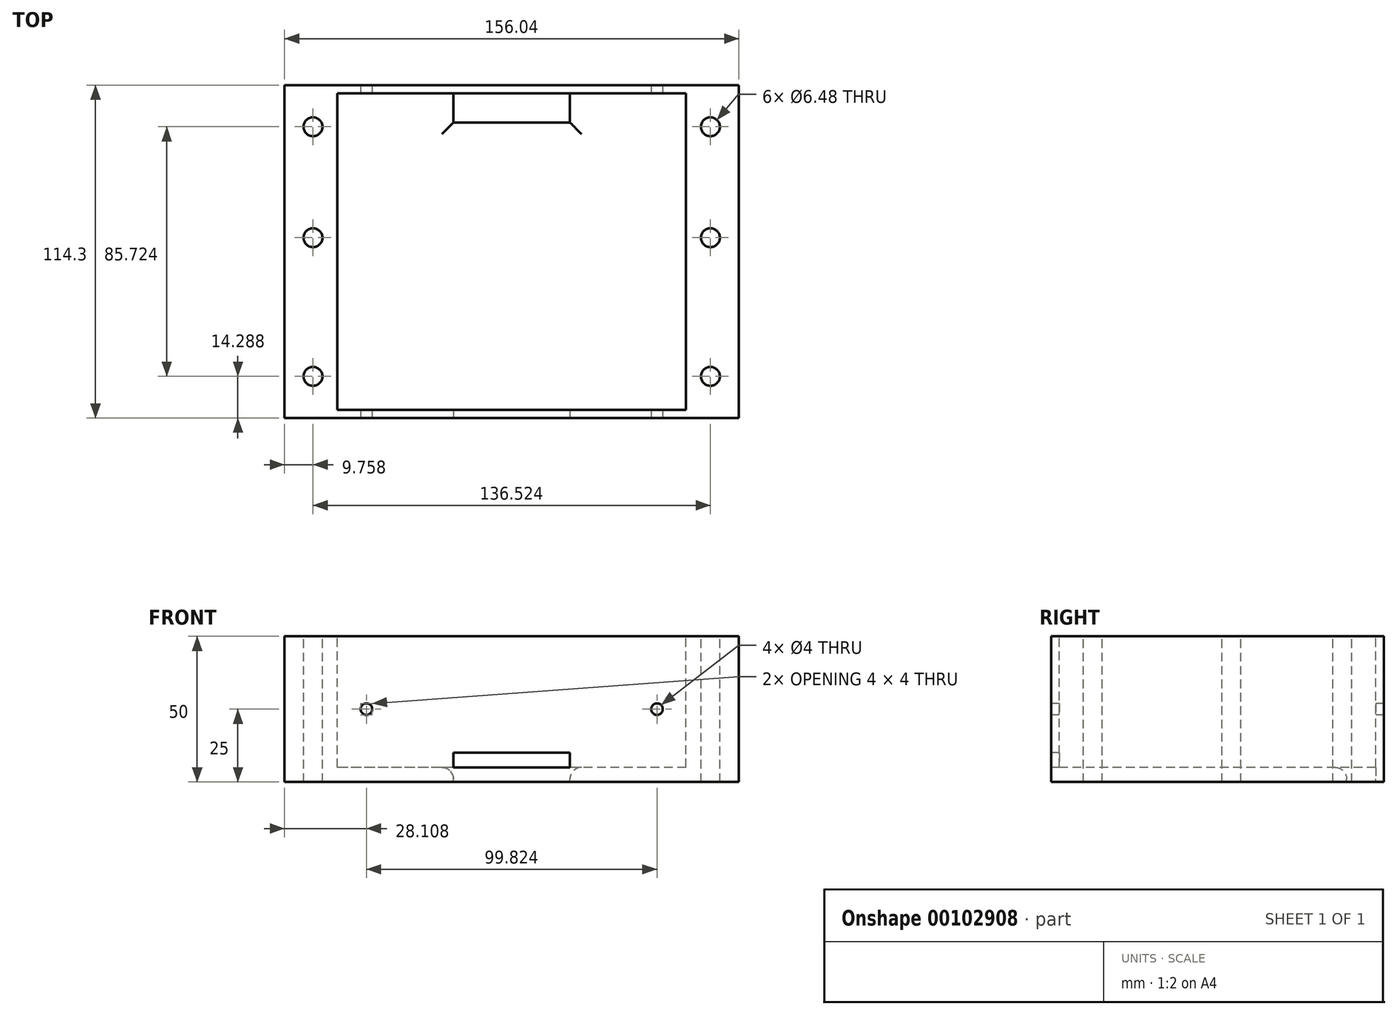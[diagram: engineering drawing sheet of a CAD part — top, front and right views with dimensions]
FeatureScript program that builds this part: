
annotation { "Feature Type Name" : "Feature", "Feature Type Description" : "" }
export const myFeature = defineFeature(function(context is Context, id is Id, definition is map)
    precondition{}
    {
        {
            var Q0;
            Q0=qCreatedBy(makeId("Top.planeOp"),FACE);
            var sketch = newSketch(context, id + "F0", { "sketchPlane" : qUnion([Q0])});
            skArc(sketch, "E0", {"start": v(-68.26, -1.59) * mm, "mid": v(-61.91, 4.76) * mm, "end": v(-68.26, 11.11) * mm});
            skArc(sketch, "E1", {"start": v(68.26, 11.11) * mm, "mid": v(61.91, 4.76) * mm, "end": v(68.26, -1.59) * mm});
            skArc(sketch, "E2", {"start": v(-68.26, 36.51) * mm, "mid": v(-61.91, 42.86) * mm, "end": v(-68.26, 49.21) * mm});
            skArc(sketch, "E3", {"start": v(-68.26, -49.21) * mm, "mid": v(-61.91, -42.86) * mm, "end": v(-68.26, -36.51) * mm});
            skArc(sketch, "E4", {"start": v(68.26, -36.51) * mm, "mid": v(61.91, -42.86) * mm, "end": v(68.26, -49.21) * mm});
            skLineSegment(sketch, "E5", {"start": v(-68.26, 36.51) * mm, "end": v(-72.23, 36.51) * mm});
            skLineSegment(sketch, "E6", {"start": v(-72.23, 11.11) * mm, "end": v(-72.23, 36.51) * mm});
            skLineSegment(sketch, "E7", {"start": v(-68.26, 11.11) * mm, "end": v(-72.23, 11.11) * mm});
            skLineSegment(sketch, "E8", {"start": v(-68.26, -1.59) * mm, "end": v(-72.23, -1.59) * mm});
            skLineSegment(sketch, "E9", {"start": v(-72.23, -36.51) * mm, "end": v(-72.23, -1.59) * mm});
            skLineSegment(sketch, "E10", {"start": v(-68.26, -36.51) * mm, "end": v(-72.23, -36.51) * mm});
            skLineSegment(sketch, "E11", {"start": v(-68.26, -49.21) * mm, "end": v(-72.23, -49.21) * mm});
            skLineSegment(sketch, "E12", {"start": v(-72.23, -56.35) * mm, "end": v(-72.23, -49.21) * mm});
            skLineSegment(sketch, "E13", {"start": v(72.22, -56.35) * mm, "end": v(-72.23, -56.35) * mm});
            skLineSegment(sketch, "E14", {"start": v(72.22, -56.35) * mm, "end": v(72.22, -49.21) * mm});
            skLineSegment(sketch, "E15", {"start": v(68.26, -49.21) * mm, "end": v(72.22, -49.21) * mm});
            skLineSegment(sketch, "E16", {"start": v(68.26, -36.51) * mm, "end": v(72.22, -36.51) * mm});
            skLineSegment(sketch, "E17", {"start": v(72.22, -36.51) * mm, "end": v(72.22, -1.59) * mm});
            skLineSegment(sketch, "E18", {"start": v(68.26, -1.59) * mm, "end": v(72.22, -1.59) * mm});
            skLineSegment(sketch, "E19", {"start": v(68.26, 11.11) * mm, "end": v(72.22, 11.11) * mm});
            skLineSegment(sketch, "E20", {"start": v(72.22, 11.11) * mm, "end": v(72.22, 36.51) * mm});
            skLineSegment(sketch, "E21", {"start": v(68.26, 36.51) * mm, "end": v(72.22, 36.51) * mm});
            skArc(sketch, "E22", {"start": v(68.26, 49.21) * mm, "mid": v(61.91, 42.86) * mm, "end": v(68.26, 36.51) * mm});
            skLineSegment(sketch, "E23", {"start": v(68.26, 49.21) * mm, "end": v(72.22, 49.21) * mm});
            skLineSegment(sketch, "E24", {"start": v(72.22, 49.21) * mm, "end": v(72.22, 56.35) * mm});
            skLineSegment(sketch, "E25", {"start": v(72.22, 56.35) * mm, "end": v(-72.23, 56.35) * mm});
            skLineSegment(sketch, "E26", {"start": v(-72.23, 49.21) * mm, "end": v(-72.23, 56.35) * mm});
            skLineSegment(sketch, "E27", {"start": v(-68.26, 49.21) * mm, "end": v(-72.23, 49.21) * mm});
            skCircle(sketch, "E28", {"center": v(-68.26, -42.86) * mm, "radius": 3.24 * mm});
            skCircle(sketch, "E29", {"center": v(68.26, 42.86) * mm, "radius": 3.24 * mm});
            skCircle(sketch, "E30", {"center": v(-68.26, 4.76) * mm, "radius": 3.24 * mm});
            skCircle(sketch, "E31", {"center": v(68.26, 4.76) * mm, "radius": 3.24 * mm});
            skLineSegment(sketch, "E32", {"start": v(73.03, -57.15) * mm, "end": v(73.03, 57.15) * mm});
            skCircle(sketch, "E33", {"center": v(-68.26, 42.86) * mm, "radius": 3.24 * mm});
            skLineSegment(sketch, "E34", {"start": v(-73.03, -57.15) * mm, "end": v(-73.03, 57.15) * mm});
            skLineSegment(sketch, "E35", {"start": v(73.03, 57.15) * mm, "end": v(-73.03, 57.15) * mm});
            skLineSegment(sketch, "E36", {"start": v(73.03, -57.15) * mm, "end": v(-73.03, -57.15) * mm});
            skCircle(sketch, "E37", {"center": v(68.26, -42.86) * mm, "radius": 3.24 * mm});
            skLineSegment(sketch, "E38.bottom", {"start": v(73.03, 57.15) * mm, "end": v(78.03, 57.15) * mm});
            skLineSegment(sketch, "E38.top", {"start": v(73.03, -57.15) * mm, "end": v(78.03, -57.15) * mm});
            skLineSegment(sketch, "E38.left", {"start": v(73.03, 57.15) * mm, "end": v(73.03, -57.15) * mm});
            skLineSegment(sketch, "E38.right", {"start": v(78.03, 57.15) * mm, "end": v(78.03, -57.15) * mm});
            skLineSegment(sketch, "E39.MirrorCS", {"start": v(-78.03, 57.15) * mm, "end": v(-78.03, -57.15) * mm});
            skLineSegment(sketch, "E40.MirrorCS", {"start": v(-73.03, 57.15) * mm, "end": v(-78.03, 57.15) * mm});
            skLineSegment(sketch, "E41.MirrorCS", {"start": v(-73.03, -57.15) * mm, "end": v(-78.03, -57.15) * mm});
            skSolve(sketch);
        }
        {
            var Q0;
            Q0 = qSketchRegion(id + "F0", true);
            var Q1;
            Q1=makeQuery(id+"F0.imprint","IMPRINT",FACE,{"disambiguationData":[TD([[makeQuery(id+"F0.imprint","IMPRINT",EDGE,{"derivedFrom":sQuery(id+"F0.wireOp",EDGE,"E30")}),-1.0]])]});
            var Q2;
            Q2=makeQuery(id+"F0.imprint","IMPRINT",FACE,{"disambiguationData":[TD([[makeQuery(id+"F0.imprint","IMPRINT",EDGE,{"derivedFrom":sQuery(id+"F0.wireOp",EDGE,"E33")}),-1.0]])]});
            var Q3;
            Q3=makeQuery(id+"F0.imprint","IMPRINT",FACE,{"disambiguationData":[TD([[makeQuery(id+"F0.imprint","IMPRINT",EDGE,{"derivedFrom":sQuery(id+"F0.wireOp",EDGE,"E29")}),-1.0]])]});
            var Q4;
            Q4=makeQuery(id+"F0.imprint","IMPRINT",FACE,{"disambiguationData":[TD([[makeQuery(id+"F0.imprint","IMPRINT",EDGE,{"derivedFrom":sQuery(id+"F0.wireOp",EDGE,"E5")}),1.0]])]});
            var Q5;
            Q5=makeQuery(id+"F0.imprint","IMPRINT",FACE,{"disambiguationData":[TD([[makeQuery(id+"F0.imprint","IMPRINT",EDGE,{"derivedFrom":sQuery(id+"F0.wireOp",EDGE,"E31")}),-1.0]])]});
            var Q6;
            Q6=makeQuery(id+"F0.imprint","IMPRINT",FACE,{"disambiguationData":[TD([[makeQuery(id+"F0.imprint","IMPRINT",EDGE,{"derivedFrom":sQuery(id+"F0.wireOp",EDGE,"E37")}),-1.0]])]});
            var Q7;
            Q7=makeQuery(id+"F0.imprint","IMPRINT",FACE,{"disambiguationData":[TD([[makeQuery(id+"F0.imprint","IMPRINT",EDGE,{"derivedFrom":sQuery(id+"F0.wireOp",EDGE,"E28")}),-1.0]])]});
            extrude(context, id + "F1", {"entities" : qUnion([Q0, Q1, Q2, Q3, Q4, Q5, Q6, Q7]), "oppositeDirection" : true, "depth" : 50 * mm});
        }
        {
            var Q0;
            Q0=makeQuery(id+"F0.imprint","IMPRINT",FACE,{"disambiguationData":[TD([[makeQuery(id+"F0.imprint","IMPRINT",EDGE,{"derivedFrom":sQuery(id+"F0.wireOp",EDGE,"E5")}),1.0]])]});
            var sketch = newSketch(context, id + "F2", { "sketchPlane" : qUnion([Q0])});
            skLineSegment(sketch, "E42.bottom", {"start": v(59.91, 54.35) * mm, "end": v(-59.91, 54.35) * mm});
            skLineSegment(sketch, "E42.top", {"start": v(59.91, -54.35) * mm, "end": v(-59.91, -54.35) * mm});
            skLineSegment(sketch, "E42.left", {"start": v(59.91, 54.35) * mm, "end": v(59.91, -54.35) * mm});
            skLineSegment(sketch, "E42.right", {"start": v(-59.91, 54.35) * mm, "end": v(-59.91, -54.35) * mm});
            skPoint(sketch, "E42.middle", {"position": v(0, 0) * mm});
            skSolve(sketch);
        }
        {
            var Q0;
            Q0 = qSketchRegion(id + "F2", true);
            extrude(context, id + "F3", {"entities" : qUnion([Q0]), "operationType" : NewBodyOperationType.REMOVE, "oppositeDirection" : true, "depth" : 45 * mm});
        }
        {
            var Q0;
            Q0=sQuery(id+"F0.wireOp",VERTEX,"E33.center");
            var Q1;
            Q1=sQuery(id+"F0.wireOp",VERTEX,"E0.center");
            var Q2;
            Q2=sQuery(id+"F0.wireOp",VERTEX,"E3.center");
            var Q3;
            Q3=sQuery(id+"F0.wireOp",VERTEX,"E4.center");
            var Q4;
            Q4=sQuery(id+"F0.wireOp",VERTEX,"E1.center");
            var Q5;
            Q5=sQuery(id+"F0.wireOp",VERTEX,"E22.center");
            var Q6;
            Q6=makeQuery(id+"F1.opExtrude","SWEPT_BODY",BODY,{"disambiguationData":[OSD([sQuery(id+"F0.wireOp",EDGE,"E36"),sQuery(id+"F0.wireOp",EDGE,"E35"),sQuery(id+"F0.wireOp",EDGE,"E38.bottom"),sQuery(id+"F0.wireOp",EDGE,"E38.top"),sQuery(id+"F0.wireOp",EDGE,"E38.right"),sQuery(id+"F0.wireOp",EDGE,"E39.MirrorCS"),sQuery(id+"F0.wireOp",EDGE,"E40.MirrorCS"),sQuery(id+"F0.wireOp",EDGE,"E41.MirrorCS")])]});
            hole(context, id + "F4", {"style" : HoleStyle.SIMPLE, "endStyle" : HoleEndStyle.BLIND, "holeDiameter" : 5.6 * mm, "holeDepth" : 20 * mm, "locations" : qUnion([Q0, Q1, Q2, Q3, Q4, Q5]), "scope" : qUnion([Q6])});
        }
        {
            var Q0;
            Q0=makeQuery(id+"F1.opExtrude","SWEPT_FACE",FACE,{"disambiguationData":[OSD([sQuery(id+"F0.wireOp",EDGE,"E36"),sQuery(id+"F0.wireOp",EDGE,"E38.top"),sQuery(id+"F0.wireOp",EDGE,"E41.MirrorCS")])]});
            var sketch = newSketch(context, id + "F5", { "sketchPlane" : qUnion([Q0])});
            skLineSegment(sketch, "E43.bottom", {"start": v(20, -40) * mm, "end": v(-20, -40) * mm});
            skLineSegment(sketch, "E43.top", {"start": v(20, -45) * mm, "end": v(-20, -45) * mm});
            skLineSegment(sketch, "E43.left", {"start": v(20, -40) * mm, "end": v(20, -45) * mm});
            skLineSegment(sketch, "E43.right", {"start": v(-20, -40) * mm, "end": v(-20, -45) * mm});
            skPoint(sketch, "E43.middle", {"position": v(0, -42.5) * mm});
            skPoint(sketch, "E44", {"position": v(-49.91, -25) * mm});
            skPoint(sketch, "E44.positionSnap0", {"position": v(-78.03, -25) * mm});
            skPoint(sketch, "E45.MirrorP", {"position": v(49.91, -25) * mm});
            skSolve(sketch);
        }
        {
            var Q0;
            Q0=makeQuery(id+"F5.imprint","IMPRINT",FACE,{"disambiguationData":[TD([[makeQuery(id+"F5.imprint","IMPRINT",EDGE,{"derivedFrom":sQuery(id+"F5.wireOp",EDGE,"E43.bottom")}),1.0]])]});
            extrude(context, id + "F6", {"entities" : qUnion([Q0]), "operationType" : NewBodyOperationType.REMOVE, "endBound" : BoundingType.UP_TO_NEXT, "oppositeDirection" : true, "depth" : 25 * mm});
        }
        {
            var Q0;
            Q0=sQuery(id+"F5.wireOp",VERTEX,"E44");
            var Q1;
            Q1=sQuery(id+"F5.wireOp",VERTEX,"E45.MirrorP");
            var Q2;
            Q2=makeQuery(id+"F1.opExtrude","SWEPT_BODY",BODY,{"disambiguationData":[OSD([sQuery(id+"F0.wireOp",EDGE,"E36"),sQuery(id+"F0.wireOp",EDGE,"E35"),sQuery(id+"F0.wireOp",EDGE,"E38.bottom"),sQuery(id+"F0.wireOp",EDGE,"E38.top"),sQuery(id+"F0.wireOp",EDGE,"E38.right"),sQuery(id+"F0.wireOp",EDGE,"E39.MirrorCS"),sQuery(id+"F0.wireOp",EDGE,"E40.MirrorCS"),sQuery(id+"F0.wireOp",EDGE,"E41.MirrorCS")])]});
            hole(context, id + "F7", {"style" : HoleStyle.SIMPLE, "endStyle" : HoleEndStyle.THROUGH, "holeDiameter" : 4 * mm, "locations" : qUnion([Q0, Q1]), "scope" : qUnion([Q2]), "isTappedThrough" : true});
        }
        {
            var Q0;
            Q0=makeQuery(id+"F0.imprint","IMPRINT",FACE,{"disambiguationData":[TD([[makeQuery(id+"F0.imprint","IMPRINT",EDGE,{"derivedFrom":sQuery(id+"F0.wireOp",EDGE,"E5")}),1.0]])]});
            var sketch = newSketch(context, id + "F8", { "sketchPlane" : qUnion([Q0])});
            skLineSegment(sketch, "E46.bottom", {"start": v(20, 54.35) * mm, "end": v(-20, 54.35) * mm});
            skLineSegment(sketch, "E46.top", {"start": v(20, 44.35) * mm, "end": v(-20, 44.35) * mm});
            skLineSegment(sketch, "E46.left", {"start": v(20, 54.35) * mm, "end": v(20, 44.35) * mm});
            skLineSegment(sketch, "E46.right", {"start": v(-20, 54.35) * mm, "end": v(-20, 44.35) * mm});
            skPoint(sketch, "E46.middle", {"position": v(0, 49.35) * mm});
            skSolve(sketch);
        }
        {
            var Q0;
            Q0 = qSketchRegion(id + "F8", true);
            extrude(context, id + "F9", {"entities" : qUnion([Q0]), "operationType" : NewBodyOperationType.REMOVE, "endBound" : BoundingType.THROUGH_ALL, "oppositeDirection" : true, "depth" : 25 * mm});
        }
        {
            var Q0;
            Q0=makeQuery(id+"F9.boolean.opBoolean","INTERSECT",EDGE,{"derivedFrom":[makeQuery(id+"F6.boolean.opBoolean","MERGE",FACE,{"derivedFrom":[makeQuery(id+"F3.boolean.opBoolean","COPY",FACE,{"derivedFrom":makeQuery(id+"F3.opExtrude","CAP_FACE",FACE,{"disambiguationData":[OSD([sQuery(id+"F2.wireOp",EDGE,"E42.bottom"),sQuery(id+"F2.wireOp",EDGE,"E42.top"),sQuery(id+"F2.wireOp",EDGE,"E42.left"),sQuery(id+"F2.wireOp",EDGE,"E42.right")])],"isStart":false})}),makeQuery(id+"F6.opExtrude","SWEPT_FACE",FACE,{"disambiguationData":[OSD([sQuery(id+"F5.wireOp",EDGE,"E43.top")])]})]}),makeQuery(id+"F9.opExtrude","SWEPT_FACE",FACE,{"disambiguationData":[OSD([sQuery(id+"F8.wireOp",EDGE,"E46.right")])]})]});
            var Q1;
            Q1=makeQuery(id+"F9.boolean.opBoolean","INTERSECT",EDGE,{"derivedFrom":[makeQuery(id+"F6.boolean.opBoolean","MERGE",FACE,{"derivedFrom":[makeQuery(id+"F3.boolean.opBoolean","COPY",FACE,{"derivedFrom":makeQuery(id+"F3.opExtrude","CAP_FACE",FACE,{"disambiguationData":[OSD([sQuery(id+"F2.wireOp",EDGE,"E42.bottom"),sQuery(id+"F2.wireOp",EDGE,"E42.top"),sQuery(id+"F2.wireOp",EDGE,"E42.left"),sQuery(id+"F2.wireOp",EDGE,"E42.right")])],"isStart":false})}),makeQuery(id+"F6.opExtrude","SWEPT_FACE",FACE,{"disambiguationData":[OSD([sQuery(id+"F5.wireOp",EDGE,"E43.top")])]})]}),makeQuery(id+"F9.opExtrude","SWEPT_FACE",FACE,{"disambiguationData":[OSD([sQuery(id+"F8.wireOp",EDGE,"E46.top")])]})]});
            var Q2;
            Q2=makeQuery(id+"F9.boolean.opBoolean","INTERSECT",EDGE,{"derivedFrom":[makeQuery(id+"F6.boolean.opBoolean","MERGE",FACE,{"derivedFrom":[makeQuery(id+"F3.boolean.opBoolean","COPY",FACE,{"derivedFrom":makeQuery(id+"F3.opExtrude","CAP_FACE",FACE,{"disambiguationData":[OSD([sQuery(id+"F2.wireOp",EDGE,"E42.bottom"),sQuery(id+"F2.wireOp",EDGE,"E42.top"),sQuery(id+"F2.wireOp",EDGE,"E42.left"),sQuery(id+"F2.wireOp",EDGE,"E42.right")])],"isStart":false})}),makeQuery(id+"F6.opExtrude","SWEPT_FACE",FACE,{"disambiguationData":[OSD([sQuery(id+"F5.wireOp",EDGE,"E43.top")])]})]}),makeQuery(id+"F9.opExtrude","SWEPT_FACE",FACE,{"disambiguationData":[OSD([sQuery(id+"F8.wireOp",EDGE,"E46.left")])]})]});
            fillet(context, id + "F10", {"entities" : qUnion([Q0, Q1, Q2]), "radius" : 4 * mm, "tangentPropagation" : true, "allowEdgeOverflow" : false});
        }
    });
